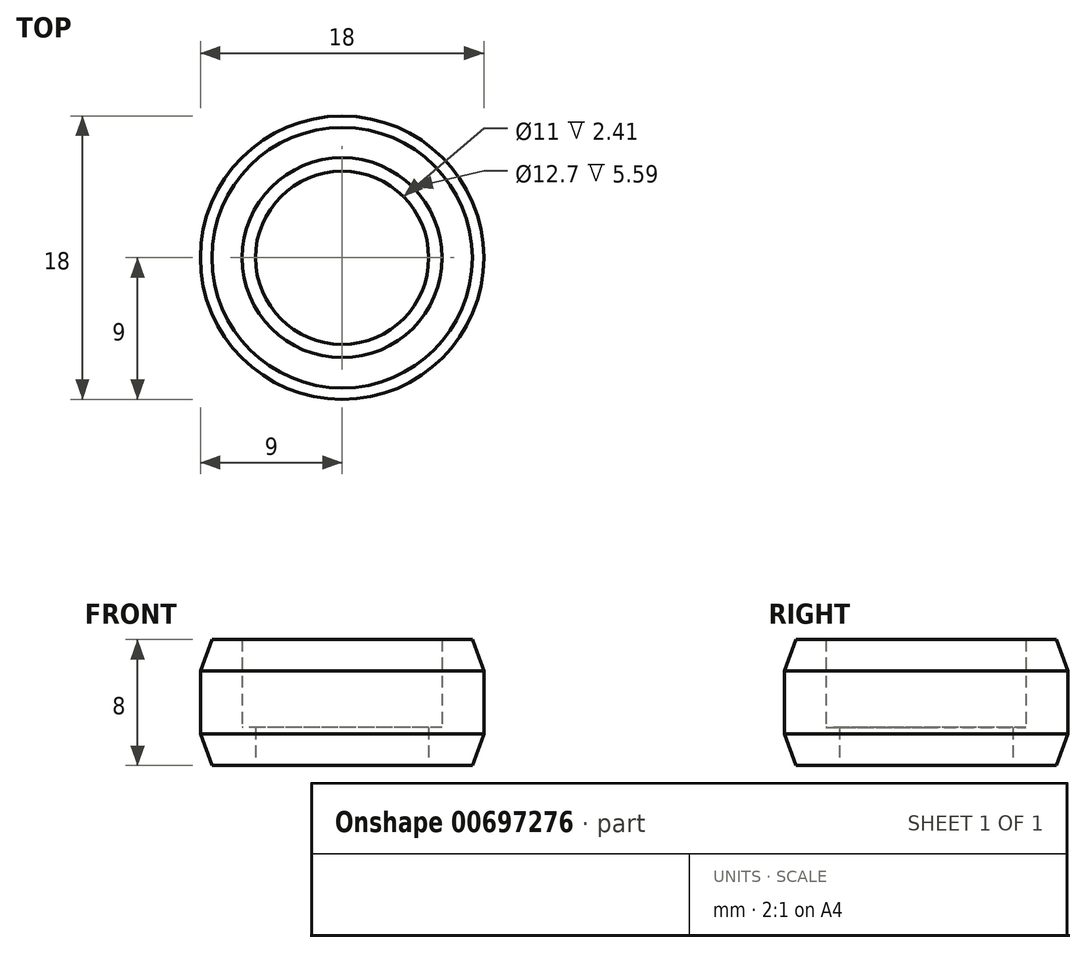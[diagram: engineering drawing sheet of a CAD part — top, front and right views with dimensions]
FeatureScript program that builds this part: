
annotation { "Feature Type Name" : "Feature", "Feature Type Description" : "" }
export const myFeature = defineFeature(function(context is Context, id is Id, definition is map)
    precondition{}
    {
        {
            var Q0;
            Q0=qCreatedBy(makeId("Top.planeOp"),FACE);
            var sketch = newSketch(context, id + "F0", { "sketchPlane" : qUnion([Q0])});
            skCircle(sketch, "E0", {"center": v(0, 0) * mm, "radius": 6.35 * mm});
            skCircle(sketch, "E1", {"center": v(0, 0) * mm, "radius": 9 * mm});
            skCircle(sketch, "E2", {"center": v(0, 0) * mm, "radius": 5.5 * mm});
            skSolve(sketch);
        }
        {
            var Q0;
            Q0=makeQuery(id+"F0.imprint","IMPRINT",FACE,{"disambiguationData":[TD([[makeQuery(id+"F0.imprint","IMPRINT",EDGE,{"derivedFrom":sQuery(id+"F0.wireOp",EDGE,"E0")}),1.0]])]});
            extrude(context, id + "F1", {"entities" : qUnion([Q0]), "depth" : 2.41 * mm, "offsetDistance" : 25 * mm});
        }
        {
            var Q0;
            Q0 = qSketchRegion(id + "F0", true);
            extrude(context, id + "F2", {"entities" : qUnion([Q0]), "operationType" : NewBodyOperationType.ADD, "depth" : 8 * mm, "offsetDistance" : 25 * mm});
        }
        {
            var Q0;
            Q0=makeQuery(id+"F2.opExtrude","CAP_EDGE",EDGE,{"disambiguationData":[OSD([sQuery(id+"F0.wireOp",EDGE,"E1")])],"isStart":true});
            chamfer(context, id + "F3", {"entities" : qUnion([Q0]), "chamferType" : ChamferType.OFFSET_ANGLE, "width" : 2 * mm, "oppositeDirection" : false, "angle" : 20 * degree, "tangentPropagation" : true});
        }
        {
            var Q0;
            Q0=makeQuery(id+"F2.opExtrude","CAP_EDGE",EDGE,{"disambiguationData":[OSD([sQuery(id+"F0.wireOp",EDGE,"E1")])],"isStart":false});
            chamfer(context, id + "F4", {"entities" : qUnion([Q0]), "chamferType" : ChamferType.OFFSET_ANGLE, "width" : 2 * mm, "oppositeDirection" : true, "angle" : 20 * degree, "tangentPropagation" : true});
        }
    });
